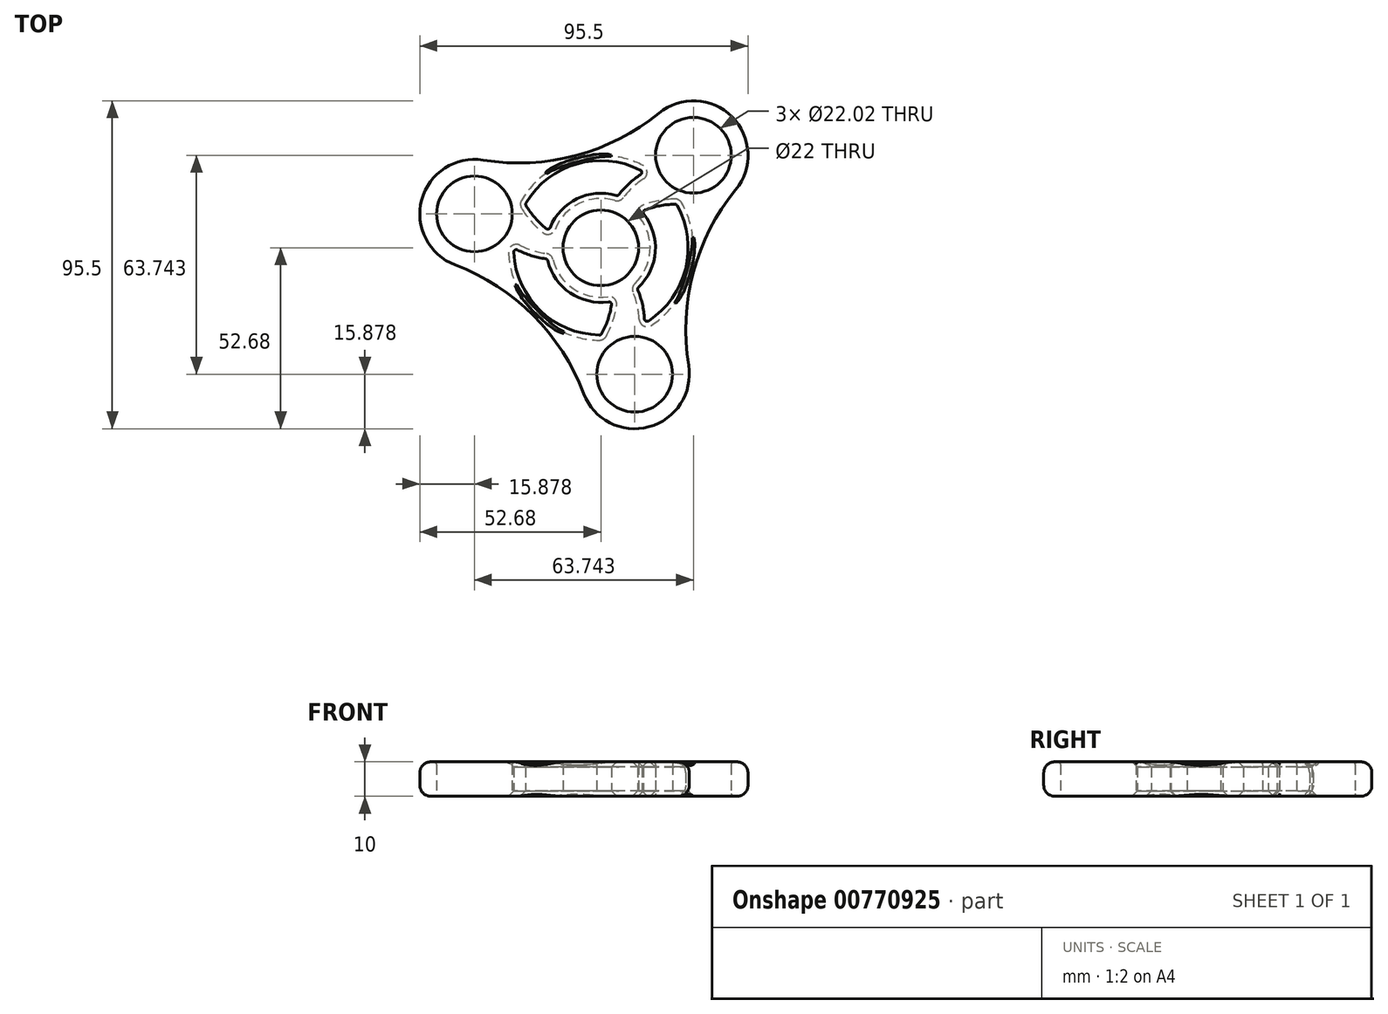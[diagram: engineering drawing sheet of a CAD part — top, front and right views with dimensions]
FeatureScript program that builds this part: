
annotation { "Feature Type Name" : "Feature", "Feature Type Description" : "" }
export const myFeature = defineFeature(function(context is Context, id is Id, definition is map)
    precondition{}
    {
        {
            var Q0;
            Q0=qCreatedBy(makeId("Top.planeOp"),FACE);
            var sketch = newSketch(context, id + "F0", { "sketchPlane" : qUnion([Q0])});
            skCircle(sketch, "E0", {"center": v(0, 0) * mm, "radius": 11 * mm});
            skArc(sketch, "E1", {"start": v(4.46, 15.24) * mm, "mid": v(-6.93, 14.28) * mm, "end": v(-14.73, 5.92) * mm});
            skArc(sketch, "E2", {"start": v(-25.36, -1.34) * mm, "mid": v(-17.64, -18.27) * mm, "end": v(-0.46, -25.4) * mm});
            skArc(sketch, "E3", {"start": v(11.6, 21.32) * mm, "mid": v(8.19, 18.68) * mm, "end": v(5.28, 15.5) * mm});
            skArc(sketch, "E4", {"start": v(21.54, 12.7) * mm, "mid": v(17.1, 12.22) * mm, "end": v(12.81, 10.98) * mm});
            skArc(sketch, "E5.1.0", {"start": v(-24.26, -0.62) * mm, "mid": v(-20.27, -2.25) * mm, "end": v(-16.06, -3.18) * mm});
            skArc(sketch, "E5.2.0", {"start": v(12.67, -20.7) * mm, "mid": v(12.08, -16.43) * mm, "end": v(10.79, -12.32) * mm});
            skArc(sketch, "E6.1.0", {"start": v(-21.77, 12.3) * mm, "mid": v(-19.14, 8.7) * mm, "end": v(-15.92, 5.6) * mm});
            skArc(sketch, "E6.2.0", {"start": v(0.22, -25) * mm, "mid": v(2.04, -20.92) * mm, "end": v(3.1, -16.59) * mm});
            skArc(sketch, "E7.trimOffspring", {"start": v(-15.42, -3.75) * mm, "mid": v(-8.9, -13.15) * mm, "end": v(2.24, -15.72) * mm});
            skArc(sketch, "E8.trimOffspring", {"start": v(10.96, -11.48) * mm, "mid": v(15.83, -1.13) * mm, "end": v(12.49, 9.8) * mm});
            skArc(sketch, "E9.trimOffspring", {"start": v(13.84, -21.3) * mm, "mid": v(24.65, -6.15) * mm, "end": v(22.22, 12.3) * mm});
            skLineSegment(sketch, "E10", {"start": v(0, 0) * mm, "end": v(40, 40) * mm, "construction": true});
            skCircle(sketch, "E11", {"center": v(26.94, 26.94) * mm, "radius": 11.01 * mm});
            skArc(sketch, "E12.trimOffspring", {"start": v(11.52, 22.64) * mm, "mid": v(-7, 24.42) * mm, "end": v(-21.77, 13.1) * mm});
            skCircle(sketch, "E13.1.0", {"center": v(-36.8, 9.86) * mm, "radius": 11.01 * mm});
            skCircle(sketch, "E13.2.0", {"center": v(9.86, -36.8) * mm, "radius": 11.01 * mm});
            skLineSegment(sketch, "E14", {"start": v(0, 0) * mm, "end": v(-36.8, 9.86) * mm, "construction": true});
            skLineSegment(sketch, "E15", {"start": v(-36.8, 9.86) * mm, "end": v(-63.77, 17.09) * mm, "construction": true});
            skLineSegment(sketch, "E16", {"start": v(0, 0) * mm, "end": v(9.86, -36.8) * mm});
            skArc(sketch, "E17", {"start": v(-34.25, 25.53) * mm, "mid": v(-7.2, 26.88) * mm, "end": v(16.9, 39.23) * mm});
            skArc(sketch, "E18.1.0", {"start": v(-4.99, -42.42) * mm, "mid": v(-19.68, -19.68) * mm, "end": v(-42.42, -4.99) * mm});
            skArc(sketch, "E18.2.0", {"start": v(39.23, 16.9) * mm, "mid": v(26.88, -7.2) * mm, "end": v(25.53, -34.25) * mm});
            skArc(sketch, "E19", {"start": v(-4.99, -42.42) * mm, "mid": v(13.97, -52.14) * mm, "end": v(25.53, -34.25) * mm});
            skArc(sketch, "E20.trimOffspring", {"start": v(-34.25, 25.53) * mm, "mid": v(-52.14, 13.97) * mm, "end": v(-42.42, -4.99) * mm});
            skArc(sketch, "E21.trimOffspring", {"start": v(39.23, 16.9) * mm, "mid": v(38.17, 38.17) * mm, "end": v(16.9, 39.23) * mm});
            skPoint(sketch, "E22.visualSharp", {"position": v(12.7, -22) * mm});
            skArc(sketch, "E22.filletArc", {"start": v(12.67, -20.7) * mm, "mid": v(13.08, -21.34) * mm, "end": v(13.84, -21.3) * mm});
            skPoint(sketch, "E23.visualSharp", {"position": v(10.58, -11.84) * mm});
            skArc(sketch, "E23.filletArc", {"start": v(10.96, -11.48) * mm, "mid": v(10.74, -11.87) * mm, "end": v(10.79, -12.32) * mm});
            skPoint(sketch, "E24.visualSharp", {"position": v(3.24, -15.54) * mm});
            skArc(sketch, "E24.filletArc", {"start": v(3.1, -16.59) * mm, "mid": v(2.9, -15.93) * mm, "end": v(2.24, -15.72) * mm});
            skPoint(sketch, "E25.visualSharp", {"position": v(0, -25.4) * mm});
            skArc(sketch, "E25.filletArc", {"start": v(-0.46, -25.4) * mm, "mid": v(-0.06, -25.3) * mm, "end": v(0.22, -25) * mm});
            skPoint(sketch, "E26.visualSharp", {"position": v(-25.4, 0) * mm});
            skArc(sketch, "E26.filletArc", {"start": v(-24.26, -0.62) * mm, "mid": v(-25.02, -0.66) * mm, "end": v(-25.36, -1.34) * mm});
            skPoint(sketch, "E27.visualSharp", {"position": v(-15.54, -3.24) * mm});
            skArc(sketch, "E27.filletArc", {"start": v(-15.42, -3.75) * mm, "mid": v(-15.66, -3.37) * mm, "end": v(-16.06, -3.18) * mm});
            skPoint(sketch, "E28.visualSharp", {"position": v(11.84, 10.58) * mm});
            skArc(sketch, "E28.filletArc", {"start": v(12.81, 10.98) * mm, "mid": v(12.35, 10.47) * mm, "end": v(12.49, 9.8) * mm});
            skPoint(sketch, "E29.visualSharp", {"position": v(22, 12.7) * mm});
            skArc(sketch, "E29.filletArc", {"start": v(22.22, 12.3) * mm, "mid": v(21.94, 12.6) * mm, "end": v(21.54, 12.7) * mm});
            skPoint(sketch, "E30.visualSharp", {"position": v(12.7, 22) * mm});
            skArc(sketch, "E30.filletArc", {"start": v(11.6, 21.32) * mm, "mid": v(11.94, 22) * mm, "end": v(11.52, 22.64) * mm});
            skPoint(sketch, "E31.visualSharp", {"position": v(4.96, 15.08) * mm});
            skArc(sketch, "E31.filletArc", {"start": v(4.46, 15.24) * mm, "mid": v(4.91, 15.24) * mm, "end": v(5.28, 15.5) * mm});
            skPoint(sketch, "E32.visualSharp", {"position": v(-15.08, 4.96) * mm});
            skArc(sketch, "E32.filletArc", {"start": v(-15.92, 5.6) * mm, "mid": v(-15.25, 5.46) * mm, "end": v(-14.73, 5.92) * mm});
            skPoint(sketch, "E33.visualSharp", {"position": v(-22, 12.7) * mm});
            skArc(sketch, "E33.filletArc", {"start": v(-21.77, 13.1) * mm, "mid": v(-21.87, 12.7) * mm, "end": v(-21.77, 12.3) * mm});
            skSolve(sketch);
        }
        {
            var Q0;
            Q0 = qSketchRegion(id + "F0", true);
            extrude(context, id + "F1", {"entities" : qUnion([Q0]), "depth" : 10 * mm, "offsetDistance" : 25.4 * mm});
        }
        {
            var Q0;
            Q0=makeQuery(id+"F1.opExtrude","CAP_EDGE",EDGE,{"disambiguationData":[OSD([sQuery(id+"F0.wireOp",EDGE,"E17")])],"isStart":false});
            var Q1;
            Q1=makeQuery(id+"F1.opExtrude","CAP_EDGE",EDGE,{"disambiguationData":[OSD([sQuery(id+"F0.wireOp",EDGE,"E17")])],"isStart":true});
            fillet(context, id + "F2", {"entities" : qUnion([Q0, Q1]), "radius" : 3.17 * mm, "tangentPropagation" : true, "allowEdgeOverflow" : false});
        }
        {
            var Q0;
            Q0=makeQuery(id+"F1.opExtrude","CAP_EDGE",EDGE,{"disambiguationData":[OSD([sQuery(id+"F0.wireOp",EDGE,"E12.trimOffspring")])],"isStart":false});
            var Q1;
            Q1=makeQuery(id+"F1.opExtrude","CAP_EDGE",EDGE,{"disambiguationData":[OSD([sQuery(id+"F0.wireOp",EDGE,"E3")])],"isStart":false});
            var Q2;
            Q2=makeQuery(id+"F1.opExtrude","CAP_EDGE",EDGE,{"disambiguationData":[OSD([sQuery(id+"F0.wireOp",EDGE,"E1")])],"isStart":false});
            var Q3;
            Q3=makeQuery(id+"F1.opExtrude","CAP_EDGE",EDGE,{"disambiguationData":[OSD([sQuery(id+"F0.wireOp",EDGE,"E6.1.0")])],"isStart":false});
            var Q4;
            Q4=makeQuery(id+"F1.opExtrude","CAP_EDGE",EDGE,{"disambiguationData":[OSD([sQuery(id+"F0.wireOp",EDGE,"E4")])],"isStart":false});
            var Q5;
            Q5=makeQuery(id+"F1.opExtrude","CAP_EDGE",EDGE,{"disambiguationData":[OSD([sQuery(id+"F0.wireOp",EDGE,"E8.trimOffspring")])],"isStart":false});
            var Q6;
            Q6=makeQuery(id+"F1.opExtrude","CAP_EDGE",EDGE,{"disambiguationData":[OSD([sQuery(id+"F0.wireOp",EDGE,"E9.trimOffspring")])],"isStart":false});
            var Q7;
            Q7=makeQuery(id+"F1.opExtrude","CAP_EDGE",EDGE,{"disambiguationData":[OSD([sQuery(id+"F0.wireOp",EDGE,"E5.2.0")])],"isStart":false});
            var Q8;
            Q8=makeQuery(id+"F1.opExtrude","CAP_EDGE",EDGE,{"disambiguationData":[OSD([sQuery(id+"F0.wireOp",EDGE,"E7.trimOffspring")])],"isStart":false});
            var Q9;
            Q9=makeQuery(id+"F1.opExtrude","CAP_EDGE",EDGE,{"disambiguationData":[OSD([sQuery(id+"F0.wireOp",EDGE,"E5.1.0")])],"isStart":false});
            var Q10;
            Q10=makeQuery(id+"F1.opExtrude","CAP_EDGE",EDGE,{"disambiguationData":[OSD([sQuery(id+"F0.wireOp",EDGE,"E2")])],"isStart":false});
            var Q11;
            Q11=makeQuery(id+"F1.opExtrude","CAP_EDGE",EDGE,{"disambiguationData":[OSD([sQuery(id+"F0.wireOp",EDGE,"E6.2.0")])],"isStart":false});
            var Q12;
            Q12=makeQuery(id+"F1.opExtrude","CAP_EDGE",EDGE,{"disambiguationData":[OSD([sQuery(id+"F0.wireOp",EDGE,"E2")])],"isStart":true});
            var Q13;
            Q13=makeQuery(id+"F1.opExtrude","CAP_EDGE",EDGE,{"disambiguationData":[OSD([sQuery(id+"F0.wireOp",EDGE,"E6.2.0")])],"isStart":true});
            var Q14;
            Q14=makeQuery(id+"F1.opExtrude","CAP_EDGE",EDGE,{"disambiguationData":[OSD([sQuery(id+"F0.wireOp",EDGE,"E7.trimOffspring")])],"isStart":true});
            var Q15;
            Q15=makeQuery(id+"F1.opExtrude","CAP_EDGE",EDGE,{"disambiguationData":[OSD([sQuery(id+"F0.wireOp",EDGE,"E5.1.0")])],"isStart":true});
            var Q16;
            Q16=makeQuery(id+"F1.opExtrude","CAP_EDGE",EDGE,{"disambiguationData":[OSD([sQuery(id+"F0.wireOp",EDGE,"E1")])],"isStart":true});
            var Q17;
            Q17=makeQuery(id+"F1.opExtrude","CAP_EDGE",EDGE,{"disambiguationData":[OSD([sQuery(id+"F0.wireOp",EDGE,"E3")])],"isStart":true});
            var Q18;
            Q18=makeQuery(id+"F1.opExtrude","CAP_EDGE",EDGE,{"disambiguationData":[OSD([sQuery(id+"F0.wireOp",EDGE,"E6.1.0")])],"isStart":true});
            var Q19;
            Q19=makeQuery(id+"F1.opExtrude","CAP_EDGE",EDGE,{"disambiguationData":[OSD([sQuery(id+"F0.wireOp",EDGE,"E9.trimOffspring")])],"isStart":true});
            var Q20;
            Q20=makeQuery(id+"F1.opExtrude","CAP_EDGE",EDGE,{"disambiguationData":[OSD([sQuery(id+"F0.wireOp",EDGE,"E5.2.0")])],"isStart":true});
            var Q21;
            Q21=makeQuery(id+"F1.opExtrude","CAP_EDGE",EDGE,{"disambiguationData":[OSD([sQuery(id+"F0.wireOp",EDGE,"E8.trimOffspring")])],"isStart":true});
            var Q22;
            Q22=makeQuery(id+"F1.opExtrude","CAP_EDGE",EDGE,{"disambiguationData":[OSD([sQuery(id+"F0.wireOp",EDGE,"E4")])],"isStart":true});
            var Q23;
            Q23=makeQuery(id+"F1.opExtrude","CAP_EDGE",EDGE,{"disambiguationData":[OSD([sQuery(id+"F0.wireOp",EDGE,"E12.trimOffspring")])],"isStart":true});
            chamfer(context, id + "F3", {"entities" : qUnion([Q0, Q1, Q2, Q3, Q4, Q5, Q6, Q7, Q8, Q9, Q10, Q11, Q12, Q13, Q14, Q15, Q16, Q17, Q18, Q19, Q20, Q21, Q22, Q23]), "width" : 1.52 * mm, "tangentPropagation" : true});
        }
        {
            var Q0;
            Q0=makeQuery(id+"F1.opExtrude","SWEPT_FACE",FACE,{"disambiguationData":[OSD([sQuery(id+"F0.wireOp",EDGE,"E11")])]});
            var Q1;
            Q1=makeQuery(id+"F1.opExtrude","CAP_FACE",FACE,{"disambiguationData":[OSD([sQuery(id+"F0.wireOp",EDGE,"E0"),sQuery(id+"F0.wireOp",EDGE,"E1"),sQuery(id+"F0.wireOp",EDGE,"E2"),sQuery(id+"F0.wireOp",EDGE,"E3"),sQuery(id+"F0.wireOp",EDGE,"E4"),sQuery(id+"F0.wireOp",EDGE,"E5.1.0"),sQuery(id+"F0.wireOp",EDGE,"E5.2.0"),sQuery(id+"F0.wireOp",EDGE,"E6.1.0"),sQuery(id+"F0.wireOp",EDGE,"E6.2.0"),sQuery(id+"F0.wireOp",EDGE,"E7.trimOffspring"),sQuery(id+"F0.wireOp",EDGE,"E8.trimOffspring"),sQuery(id+"F0.wireOp",EDGE,"E9.trimOffspring"),sQuery(id+"F0.wireOp",EDGE,"E11"),sQuery(id+"F0.wireOp",EDGE,"E12.trimOffspring"),sQuery(id+"F0.wireOp",EDGE,"E13.1.0"),sQuery(id+"F0.wireOp",EDGE,"E13.2.0"),sQuery(id+"F0.wireOp",EDGE,"E17"),sQuery(id+"F0.wireOp",EDGE,"E18.1.0"),sQuery(id+"F0.wireOp",EDGE,"E18.2.0"),sQuery(id+"F0.wireOp",EDGE,"E19"),sQuery(id+"F0.wireOp",EDGE,"E20.trimOffspring"),sQuery(id+"F0.wireOp",EDGE,"E21.trimOffspring")])],"isStart":false});
            fillet(context, id + "F4", {"entities" : qUnion([Q0, Q1]), "radius" : 0.76 * mm, "tangentPropagation" : true, "allowEdgeOverflow" : false});
        }
    });
